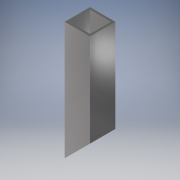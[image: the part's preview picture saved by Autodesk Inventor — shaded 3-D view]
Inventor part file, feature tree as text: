
AUTODESK INVENTOR PART (.ipt)
format: ipt  version: 2019 (Build 230136000, 136)  size: 118,272 bytes
history: native  units: mm
features: extrude x2, sketch x2, projected_geometry x1
ambient origin geometry x8: Origin, YZ Plane, XZ Plane, XY Plane, X Axis, Y Axis, Z Axis, Center Point
bodies: Solid1 (feature_tree)
feature tree (5):
  extrude  "Extrusion1"  Depth=30.0mm
  extrude  "Extrusion2"  Depth=2.5mm
  sketch  "Sketch1"  dims[d0=30.0mm d1=30.0mm]
  sketch  "Sketch2"  dims[d2=2.5mm d3=2.5mm d4=140.0mm d5=0.0mm d6=45.0deg d7=0.0mm d8=0.0mm d9=0.0mm]
  projected_geometry  "Projected Loop1"
